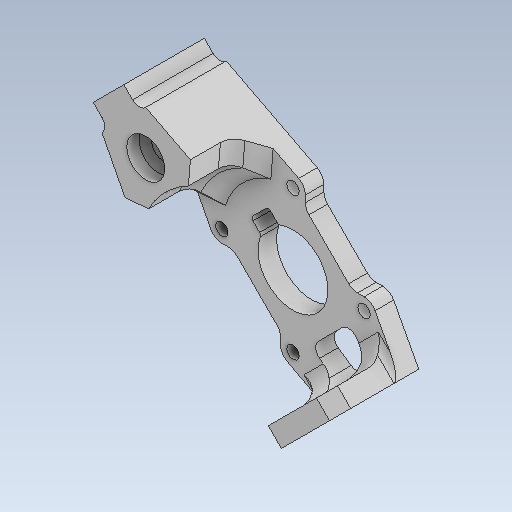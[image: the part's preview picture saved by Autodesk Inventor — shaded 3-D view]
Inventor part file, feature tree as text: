
AUTODESK INVENTOR PART (.ipt)
format: ipt  version: 2023 (Build 270158000, 158)  size: 344,576 bytes
history: native  units: mm
features: sketch x9, other x3, plane x2
ambient origin geometry x8: Origin, YZ Plane, XZ Plane, XY Plane, X Axis, Y Axis, Z Axis, Center Point
bodies: Solid1 (feature_tree)
feature tree (14):
  other  "mot_holder_1.ipt"
  other  "Solid1::mot_holder_1.ipt"
  other  "TaggingFeature1"
  sketch  "Sketch1"  dims[d0=10.0mm]
  sketch  "Sketch2"
  sketch  "Sketch3"
  sketch  "Sketch4"
  sketch  "Sketch10"
  sketch  "Sketch11"
  sketch  "Sketch12"
  sketch  "Sketch13"
  sketch  "Sketch14"
  plane  "Work Plane1"
  plane  "Work Plane2"
